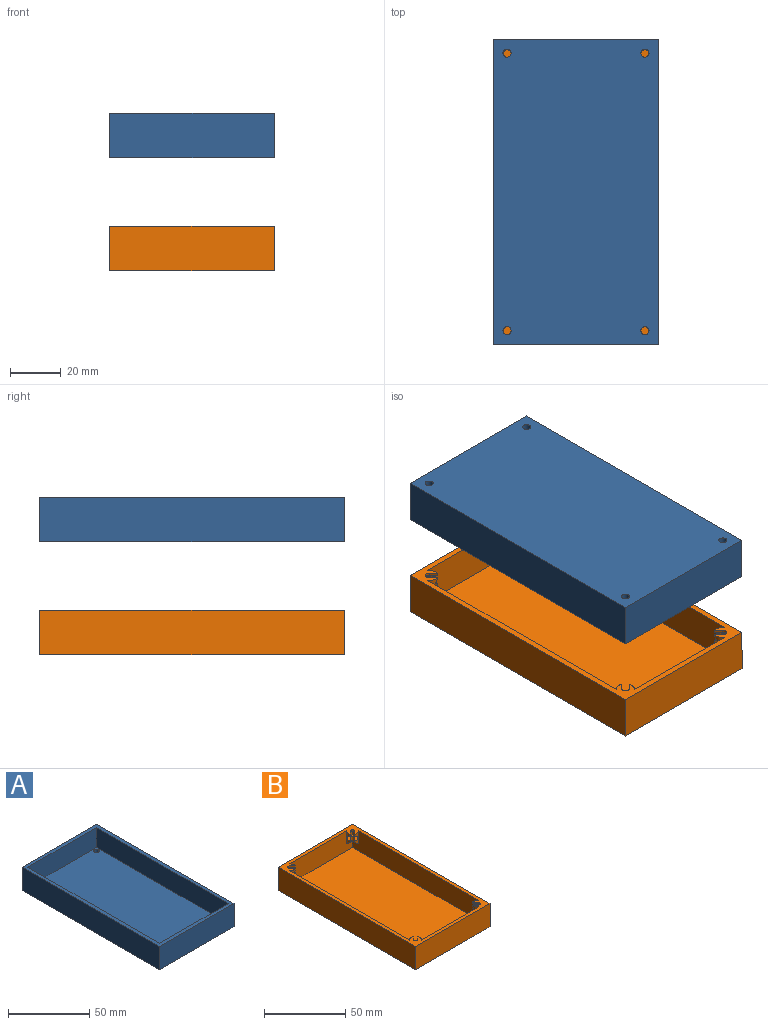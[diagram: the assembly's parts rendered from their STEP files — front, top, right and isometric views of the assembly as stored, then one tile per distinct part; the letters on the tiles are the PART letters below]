
ASSEMBLY  parts=2 mates=2
PART A: 15 faces, bbox 65x120x17.5 mm
  f0: plane 65x17.5mm, normal (0,1,0), area 1137.5mm2, adj f1,f3,f4,f9
  f1: plane 120x17.5mm, normal (-1,0,0), area 2100mm2, adj f0,f2,f4,f9
  f2: plane 65x17.5mm, normal (0,-1,0), area 1137.5mm2, adj f1,f3,f4,f9
  f3: plane 120x17.5mm, normal (1,0,0), area 2100mm2, adj f0,f2,f4,f9
  f4: plane 120x65mm, normal (0,0,-1), area 7767.8mm2, adj f0,f1,f2,f3,f11,f12,f13,f14
  f5: plane 115x15mm, normal (1,0,0), area 1725mm2, adj f6,f8,f9,f10
  f6: plane 60x15mm, normal (0,-1,0), area 900mm2, adj f5,f7,f9,f10
  f7: plane 115x15mm, normal (-1,0,0), area 1725mm2, adj f6,f8,f9,f10
  f8: plane 60x15mm, normal (0,1,0), area 900mm2, adj f5,f7,f9,f10
  f9: plane 120x65mm, normal (0,0,1), area 900mm2, adj f0,f1,f2,f3,f5,f6,f7,f8
  f10: plane 115x60mm, normal (0,0,1), area 6867.8mm2, adj f5,f6,f7,f8,f11,f12,f13,f14
  f11: cylinder r=1.6mm len=3.2mm, axis (0,0,1), area 25.1mm2, adj f4,f10
  f12: cylinder r=1.6mm len=3.2mm, axis (0,0,1), area 25.1mm2, adj f4,f10
  f13: cylinder r=1.6mm len=3.2mm, axis (0,0,1), area 25.1mm2, adj f4,f10
  f14: cylinder r=1.6mm len=3.2mm, axis (0,0,1), area 25.1mm2, adj f4,f10
PART B: 99 faces, bbox 65x120x17.5 mm
  f0: plane 0.23x0.17mm, normal (0,0,-1), area 0mm2, adj f4,f5,f98
  f1: cylinder r=3.5mm len=9.9mm, axis (0,0,1), area 30.6mm2, adj f2,f12,f33,f83,f86,f87,f89,f96
  f2: plane 3.09x2.24mm, normal (-0.71,-0.71,0), area 6.4mm2, adj f1,f3,f86,f87,f97
  f3: cylinder r=1.5mm len=3.52mm, axis (0,0,1), area 15.9mm2, adj f2,f4,f87,f97,f98
  f4: plane 3.09x2.24mm, normal (0.71,0.71,0), area 6.4mm2, adj f0,f3,f5,f87,f98
  f5: cylinder r=3.5mm len=9.9mm, axis (0,0,1), area 30.6mm2, adj f0,f4,f19,f33,f85,f87,f90,f93
  f6: plane 0.23x0.17mm, normal (0,0,-1), area 0mm2, adj f7,f8,f82
  f7: cylinder r=3.5mm len=9.9mm, axis (0,0,1), area 30.6mm2, adj f6,f8,f27,f33,f67,f74,f75,f77
  f8: plane 3.09x2.24mm, normal (0.71,-0.71,0), area 6.4mm2, adj f6,f7,f9,f75,f82
  f9: cylinder r=1.5mm len=3.52mm, axis (0,0,1), area 15.9mm2, adj f8,f10,f75,f81,f82
  f10: plane 3.09x2.24mm, normal (-0.71,0.71,0), area 6.4mm2, adj f9,f11,f70,f75,f81
  f11: cylinder r=3.5mm len=9.9mm, axis (0,0,1), area 30.6mm2, adj f10,f12,f33,f69,f70,f71,f75,f80
  f12: plane 115x15mm, normal (-1,0,0), area 1628.2mm2, adj f1,f11,f19,f27,f33,f34,f81,f97
  f13: plane 0.23x0.17mm, normal (0,0,-1), area 0mm2, adj f14,f15,f66
  f14: cylinder r=3.5mm len=9.9mm, axis (0,0,1), area 30.6mm2, adj f13,f15,f19,f33,f51,f58,f59,f61
  f15: plane 3.09x2.24mm, normal (-0.71,0.71,0), area 6.4mm2, adj f13,f14,f16,f59,f66
  f16: cylinder r=1.5mm len=3.52mm, axis (0,0,1), area 15.9mm2, adj f15,f17,f59,f65,f66
  f17: plane 3.09x2.24mm, normal (0.71,-0.71,0), area 6.4mm2, adj f16,f18,f54,f59,f65
  f18: cylinder r=3.5mm len=9.9mm, axis (0,0,1), area 30.6mm2, adj f17,f26,f33,f53,f54,f55,f59,f64
  f19: plane 60x15mm, normal (0,1,0), area 803.2mm2, adj f5,f12,f14,f26,f33,f34,f66,f98
  f20: plane 0.23x0.17mm, normal (0,0,-1), area 0mm2, adj f24,f25,f50
  f21: cylinder r=3.5mm len=9.9mm, axis (0,0,1), area 30.6mm2, adj f22,f26,f33,f35,f38,f39,f41,f48
  f22: plane 3.09x2.24mm, normal (0.71,0.71,0), area 6.4mm2, adj f21,f23,f38,f39,f49
  f23: cylinder r=1.5mm len=3.52mm, axis (0,0,1), area 15.9mm2, adj f22,f24,f39,f49,f50
  f24: plane 3.09x2.24mm, normal (-0.71,-0.71,0), area 6.4mm2, adj f20,f23,f25,f39,f50
  f25: cylinder r=3.5mm len=9.9mm, axis (0,0,1), area 30.6mm2, adj f20,f24,f27,f33,f37,f39,f42,f45
  f26: plane 115x15mm, normal (1,0,0), area 1628.2mm2, adj f18,f19,f21,f27,f33,f34,f49,f65
  f27: plane 60x15mm, normal (0,-1,0), area 803.2mm2, adj f7,f12,f25,f26,f33,f34,f50,f82
  f28: plane 65x17.5mm, normal (0,1,0), area 1137.5mm2, adj f29,f31,f32,f33
  f29: plane 120x17.5mm, normal (-1,0,0), area 2100mm2, adj f28,f30,f32,f33
  f30: plane 65x17.5mm, normal (0,-1,0), area 1137.5mm2, adj f29,f31,f32,f33
  f31: plane 120x17.5mm, normal (1,0,0), area 2100mm2, adj f28,f30,f32,f33
  f32: plane 120x65mm, normal (0,0,-1), area 7800mm2, adj f28,f29,f30,f31
  f33: plane 120x65mm, normal (0,0,1), area 985.1mm2, adj f1,f5,f7,f11,f12,f14,f18,f19
  f34: plane 115x60mm, normal (0,0,1), area 6900mm2, adj f12,f19,f26,f27
  f35: plane 2.24x2.24mm, normal (0.71,0.71,0), area 3.6mm2, adj f21,f33,f36,f48
  f36: cylinder r=1.5mm len=2.56mm, axis (0,0,1), area 4.8mm2, adj f33,f35,f37,f40,f45,f48
  f37: plane 2.24x2.24mm, normal (-0.71,-0.71,0), area 3.6mm2, adj f25,f33,f36,f45
  f38: plane 0.23x0.17mm, normal (0,0,-1), area 0mm2, adj f21,f22,f49
  f39: plane 6.83x6.83mm, normal (0,0,1), area 19.1mm2, adj f21,f22,f23,f24,f25,f41,f42,f43
  f40: plane 2.16x2.16mm, normal (0,0,-1), area 0.3mm2, adj f36,f45,f46,f47,f48
  f41: plane 2.74x2.74mm, normal (0.71,0.71,0), area 10.1mm2, adj f21,f39,f44,f48
  f42: plane 2.74x2.74mm, normal (-0.71,-0.71,0), area 10.1mm2, adj f25,f39,f43,f45
  f43: plane 3.19x2.6mm, normal (0.26,-0.97,0), area 8.6mm2, adj f39,f42,f44,f46
  f44: plane 3.19x2.6mm, normal (0.97,-0.26,0), area 8.6mm2, adj f39,f41,f43,f47
  f45: plane 4.5x3.24mm, normal (-0.5,-0.5,-0.71), area 8.1mm2, adj f25,f36,f37,f40,f42,f46
  f46: plane 3.19x2.08mm, normal (0.18,-0.68,-0.71), area 5.2mm2, adj f40,f43,f45,f47
  f47: plane 3.19x2.08mm, normal (0.68,-0.18,-0.71), area 5.2mm2, adj f40,f44,f46,f48
  f48: plane 4.5x3.24mm, normal (0.5,0.5,-0.71), area 8.1mm2, adj f21,f35,f36,f40,f41,f47
  f49: plane 6.33x3.83mm, normal (0.69,0,-0.72), area 14.8mm2, adj f21,f22,f23,f26,f38,f50
  f50: plane 6.33x3.83mm, normal (0,-0.69,-0.72), area 14.8mm2, adj f20,f23,f24,f25,f27,f49
  f51: plane 2.24x2.24mm, normal (-0.71,0.71,0), area 3.6mm2, adj f14,f33,f52,f61
  f52: cylinder r=1.5mm len=2.56mm, axis (0,0,1), area 4.8mm2, adj f33,f51,f53,f60,f61,f64
  f53: plane 2.24x2.24mm, normal (0.71,-0.71,0), area 3.6mm2, adj f18,f33,f52,f64
  f54: plane 0.23x0.17mm, normal (0,0,-1), area 0mm2, adj f17,f18,f65
  f55: plane 2.74x2.74mm, normal (0.71,-0.71,0), area 10.1mm2, adj f18,f56,f59,f64
  f56: plane 3.19x2.6mm, normal (0.97,0.26,0), area 8.6mm2, adj f55,f57,f59,f63
  f57: plane 3.19x2.6mm, normal (0.26,0.97,0), area 8.6mm2, adj f56,f58,f59,f62
  f58: plane 2.74x2.74mm, normal (-0.71,0.71,0), area 10.1mm2, adj f14,f57,f59,f61
  f59: plane 6.83x6.83mm, normal (0,0,1), area 19.1mm2, adj f14,f15,f16,f17,f18,f55,f56,f57
  f60: plane 2.16x2.16mm, normal (0,0,-1), area 0.3mm2, adj f52,f61,f62,f63,f64
  f61: plane 4.5x3.24mm, normal (-0.5,0.5,-0.71), area 8.1mm2, adj f14,f51,f52,f58,f60,f62
  f62: plane 3.19x2.08mm, normal (0.18,0.68,-0.71), area 5.2mm2, adj f57,f60,f61,f63
  f63: plane 3.19x2.08mm, normal (0.68,0.18,-0.71), area 5.2mm2, adj f56,f60,f62,f64
  f64: plane 4.5x3.24mm, normal (0.5,-0.5,-0.71), area 8.1mm2, adj f18,f52,f53,f55,f60,f63
  f65: plane 6.33x3.83mm, normal (0.69,0,-0.72), area 14.8mm2, adj f16,f17,f18,f26,f54,f66
  f66: plane 6.33x3.83mm, normal (0,0.69,-0.72), area 14.8mm2, adj f13,f14,f15,f16,f19,f65
  f67: plane 2.24x2.24mm, normal (0.71,-0.71,0), area 3.6mm2, adj f7,f33,f68,f77
  f68: cylinder r=1.5mm len=2.56mm, axis (0,0,1), area 4.8mm2, adj f33,f67,f69,f76,f77,f80
  f69: plane 2.24x2.24mm, normal (-0.71,0.71,0), area 3.6mm2, adj f11,f33,f68,f80
  f70: plane 0.23x0.17mm, normal (0,0,-1), area 0mm2, adj f10,f11,f81
  f71: plane 2.74x2.74mm, normal (-0.71,0.71,0), area 10.1mm2, adj f11,f72,f75,f80
  f72: plane 3.19x2.6mm, normal (-0.97,-0.26,0), area 8.6mm2, adj f71,f73,f75,f79
  f73: plane 3.19x2.6mm, normal (-0.26,-0.97,0), area 8.6mm2, adj f72,f74,f75,f78
  f74: plane 2.74x2.74mm, normal (0.71,-0.71,0), area 10.1mm2, adj f7,f73,f75,f77
  f75: plane 6.83x6.83mm, normal (0,0,1), area 19.1mm2, adj f7,f8,f9,f10,f11,f71,f72,f73
  f76: plane 2.16x2.16mm, normal (0,0,-1), area 0.3mm2, adj f68,f77,f78,f79,f80
  f77: plane 4.5x3.24mm, normal (0.5,-0.5,-0.71), area 8.1mm2, adj f7,f67,f68,f74,f76,f78
  f78: plane 3.19x2.08mm, normal (-0.18,-0.68,-0.71), area 5.2mm2, adj f73,f76,f77,f79
  f79: plane 3.19x2.08mm, normal (-0.68,-0.18,-0.71), area 5.2mm2, adj f72,f76,f78,f80
  f80: plane 4.5x3.24mm, normal (-0.5,0.5,-0.71), area 8.1mm2, adj f11,f68,f69,f71,f76,f79
  f81: plane 6.33x3.83mm, normal (-0.69,0,-0.72), area 14.8mm2, adj f9,f10,f11,f12,f70,f82
  f82: plane 6.33x3.83mm, normal (0,-0.69,-0.72), area 14.8mm2, adj f6,f7,f8,f9,f27,f81
  f83: plane 2.24x2.24mm, normal (-0.71,-0.71,0), area 3.6mm2, adj f1,f33,f84,f96
  f84: cylinder r=1.5mm len=2.56mm, axis (0,0,1), area 4.8mm2, adj f33,f83,f85,f88,f93,f96
  f85: plane 2.24x2.24mm, normal (0.71,0.71,0), area 3.6mm2, adj f5,f33,f84,f93
  f86: plane 0.23x0.17mm, normal (0,0,-1), area 0mm2, adj f1,f2,f97
  f87: plane 6.83x6.83mm, normal (0,0,1), area 19.1mm2, adj f1,f2,f3,f4,f5,f89,f90,f91
  f88: plane 2.16x2.16mm, normal (0,0,-1), area 0.3mm2, adj f84,f93,f94,f95,f96
  f89: plane 2.74x2.74mm, normal (-0.71,-0.71,0), area 10.1mm2, adj f1,f87,f92,f96
  f90: plane 2.74x2.74mm, normal (0.71,0.71,0), area 10.1mm2, adj f5,f87,f91,f93
  f91: plane 3.19x2.6mm, normal (-0.26,0.97,0), area 8.6mm2, adj f87,f90,f92,f94
  f92: plane 3.19x2.6mm, normal (-0.97,0.26,0), area 8.6mm2, adj f87,f89,f91,f95
  f93: plane 4.5x3.24mm, normal (0.5,0.5,-0.71), area 8.1mm2, adj f5,f84,f85,f88,f90,f94
  f94: plane 3.19x2.08mm, normal (-0.18,0.68,-0.71), area 5.2mm2, adj f88,f91,f93,f95
  f95: plane 3.19x2.08mm, normal (-0.68,0.18,-0.71), area 5.2mm2, adj f88,f92,f94,f96
  f96: plane 4.5x3.24mm, normal (-0.5,-0.5,-0.71), area 8.1mm2, adj f1,f83,f84,f88,f89,f95
  f97: plane 6.33x3.83mm, normal (-0.69,0,-0.72), area 14.8mm2, adj f1,f2,f3,f12,f86,f98
  f98: plane 6.33x3.83mm, normal (0,0.69,-0.72), area 14.8mm2, adj f0,f3,f4,f5,f19,f97
PLACE A rot(axis=(1,0,0),180deg) t=(-10.87,-9.33,62.83)mm
PLACE B rot(axis=(0,0,-1),180deg) t=(-10.87,-9.33,0.9)mm
MATE cylindrical A.f13 <-> B.f21  axis (0,0,-1) through (16.3,-64,62.83)mm
MATE cylindrical A.f12 <-> B.f1  axis (0,0,-1) through (-38.04,45.34,62.83)mm
